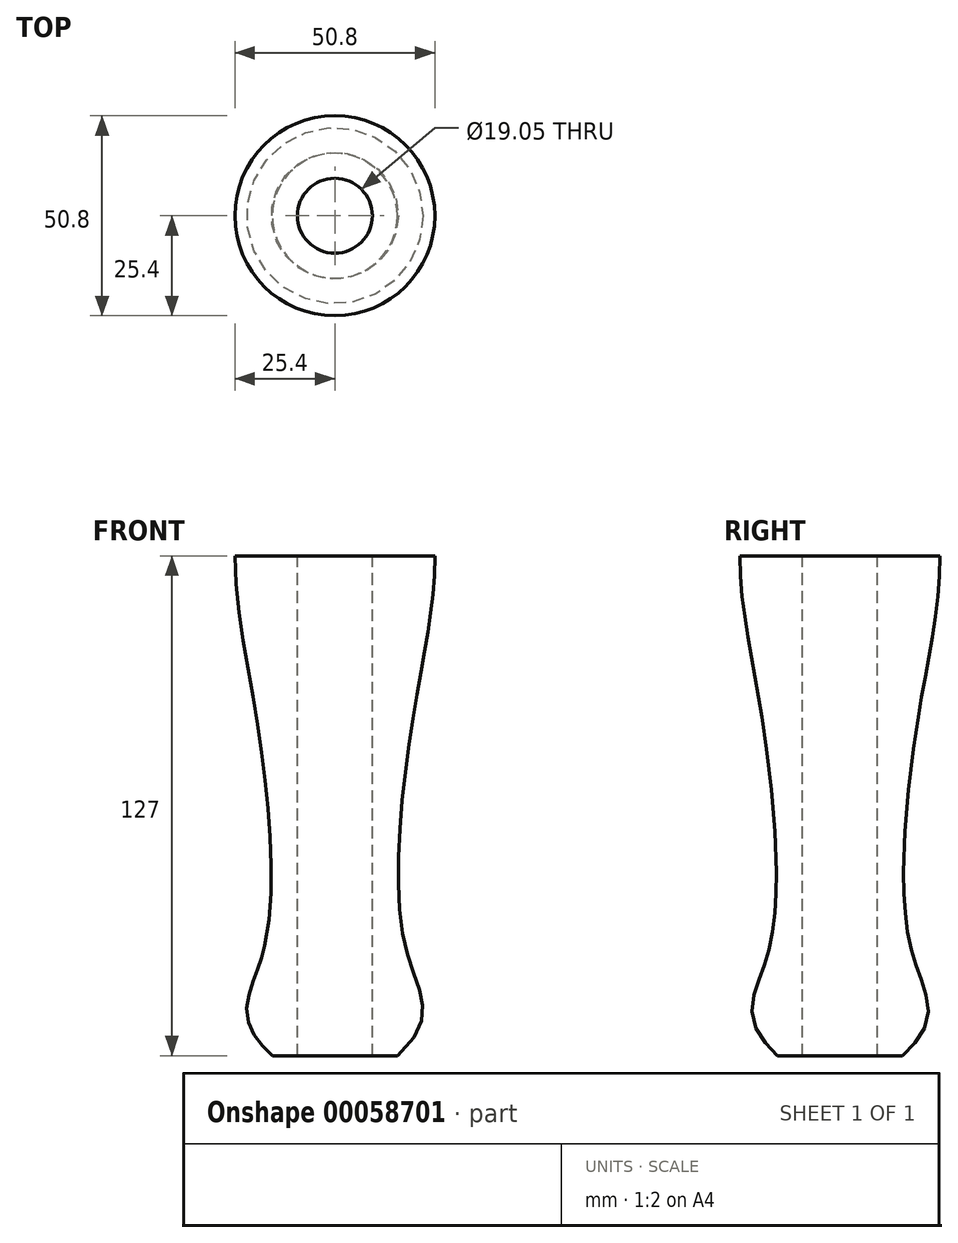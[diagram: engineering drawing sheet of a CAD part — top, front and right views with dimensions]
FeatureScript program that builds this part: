
annotation { "Feature Type Name" : "Feature", "Feature Type Description" : "" }
export const myFeature = defineFeature(function(context is Context, id is Id, definition is map)
    precondition{}
    {
        {
            var Q0;
            Q0=qCreatedBy(makeId("Front.planeOp"),FACE);
            var sketch = newSketch(context, id + "F0", { "sketchPlane" : qUnion([Q0])});
            skLineSegment(sketch, "E0", {"start": v(0, 76.2) * mm, "end": v(0, -76.2) * mm, "construction": true});
            skLineSegment(sketch, "E1", {"start": v(-76.2, 0) * mm, "end": v(76.2, 0) * mm, "construction": true});
            skLineSegment(sketch, "E2", {"start": v(9.53, -63.5) * mm, "end": v(9.52, 63.5) * mm});
            skLineSegment(sketch, "E3", {"start": v(9.53, 63.5) * mm, "end": v(25.4, 63.5) * mm});
            skLineSegment(sketch, "E4", {"start": v(9.53, -63.5) * mm, "end": v(15.88, -63.5) * mm});
            skFitSpline(sketch, "E5", {"points": [v(25.4, 63.5) * mm, v(20.54, 26.52) * mm, v(18.18, -36.94) * mm, v(15.88, -63.5) * mm], "startDerivative": vector(0, -118.15) * mm, "endDerivative": vector(-125.67, -113.82) * mm});
            skSolve(sketch);
        }
        {
            var Q0;
            Q0 = qSketchRegion(id + "F0", true);
            var Q1;
            Q1=sQuery(id+"F0.wireOp",EDGE,"E0");
            revolve(context, id + "F1", {"entities" : qUnion([Q0]), "axis" : qUnion([Q1]), "revolveType" : RevolveType.FULL});
        }
    });
